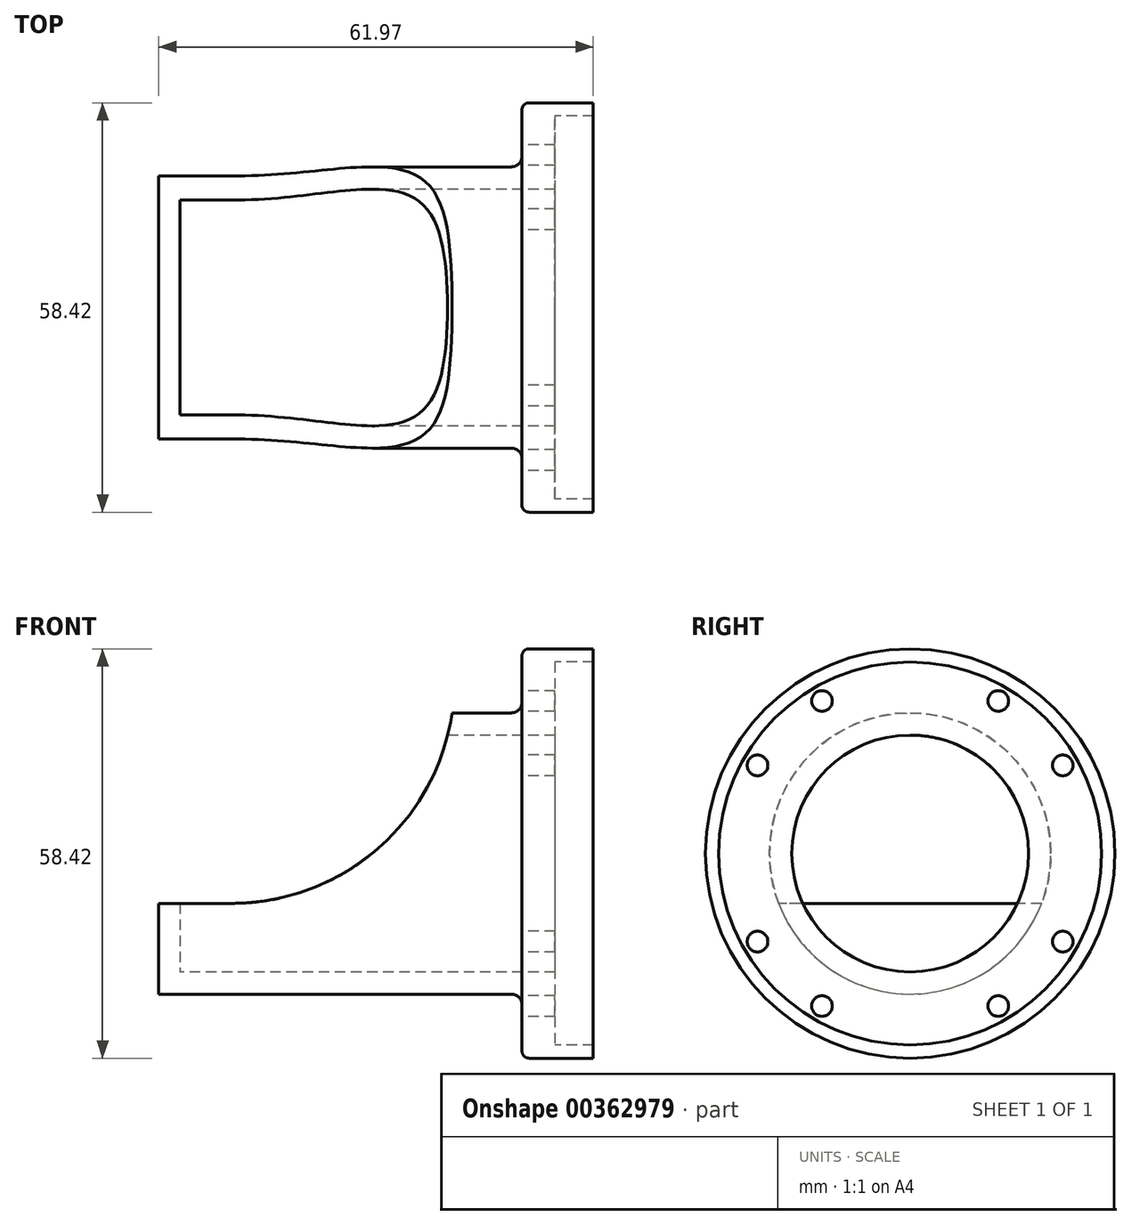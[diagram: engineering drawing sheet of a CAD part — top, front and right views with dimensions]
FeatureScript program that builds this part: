
annotation { "Feature Type Name" : "Feature", "Feature Type Description" : "" }
export const myFeature = defineFeature(function(context is Context, id is Id, definition is map)
    precondition{}
    {
        {
            var Q0;
            Q0=qCreatedBy(makeId("Front.planeOp"),FACE);
            var sketch = newSketch(context, id + "F0", { "sketchPlane" : qUnion([Q0])});
            skLineSegment(sketch, "E0", {"start": v(-33.27, -5.62) * mm, "end": v(17.02, -5.62) * mm});
            skLineSegment(sketch, "E1", {"start": v(18.54, -7.15) * mm, "end": v(18.54, -13.75) * mm});
            skLineSegment(sketch, "E2", {"start": v(19.56, -14.77) * mm, "end": v(28.7, -14.77) * mm});
            skLineSegment(sketch, "E3", {"start": v(28.7, -14.77) * mm, "end": v(28.7, -12.87) * mm});
            skLineSegment(sketch, "E4", {"start": v(28.7, -12.87) * mm, "end": v(23.24, -12.87) * mm});
            skLineSegment(sketch, "E5", {"start": v(23.24, -12.87) * mm, "end": v(23.24, -2.45) * mm});
            skLineSegment(sketch, "E6", {"start": v(23.24, -2.45) * mm, "end": v(-30.22, -2.45) * mm});
            skLineSegment(sketch, "E7", {"start": v(-30.22, -2.45) * mm, "end": v(-30.22, 12.92) * mm});
            skLineSegment(sketch, "E8", {"start": v(-30.22, 12.92) * mm, "end": v(-33.27, 12.92) * mm});
            skLineSegment(sketch, "E9", {"start": v(-33.27, 12.92) * mm, "end": v(-33.27, -5.62) * mm});
            skLineSegment(sketch, "E10", {"start": v(-34.84, 14.44) * mm, "end": v(22.49, 14.44) * mm, "construction": true});
            skPoint(sketch, "E11.visualSharp", {"position": v(18.54, -5.62) * mm});
            skArc(sketch, "E11.filletArc", {"start": v(18.54, -7.15) * mm, "mid": v(18.1, -6.07) * mm, "end": v(17.02, -5.62) * mm});
            skPoint(sketch, "E12.visualSharp", {"position": v(18.54, -14.77) * mm});
            skArc(sketch, "E12.filletArc", {"start": v(18.54, -13.75) * mm, "mid": v(18.84, -14.47) * mm, "end": v(19.56, -14.77) * mm});
            skSolve(sketch);
        }
        {
            var Q0;
            Q0=makeQuery(id+"F0.imprint","IMPRINT",FACE,{"disambiguationData":[TD([[makeQuery(id+"F0.imprint","IMPRINT",EDGE,{"derivedFrom":sQuery(id+"F0.wireOp",EDGE,"E0")}),1.0]])]});
            var Q1;
            Q1=sQuery(id+"F0.wireOp",EDGE,"E10");
            revolve(context, id + "F1", {"entities" : qUnion([Q0]), "axis" : qUnion([Q1]), "revolveType" : RevolveType.FULL});
        }
        {
            var Q0;
            Q0=qCreatedBy(makeId("Front.planeOp"),FACE);
            var sketch = newSketch(context, id + "F2", { "sketchPlane" : qUnion([Q0])});
            skLineSegment(sketch, "E13", {"start": v(8.9, 42.08) * mm, "end": v(8.9, 39.08) * mm});
            skLineSegment(sketch, "E14.0", {"start": v(-33.27, -5.62) * mm, "end": v(-33.27, 34.51) * mm});
            skLineSegment(sketch, "E15.0", {"start": v(-33.27, 7.33) * mm, "end": v(-22.86, 7.33) * mm});
            skLineSegment(sketch, "E16.0", {"start": v(18.54, -13.75) * mm, "end": v(18.54, 42.64) * mm});
            skPoint(sketch, "E17.visualSharp", {"position": v(8.9, 7.33) * mm});
            skArc(sketch, "E17.filletArc", {"start": v(-22.86, 7.33) * mm, "mid": v(-0.4, 16.63) * mm, "end": v(8.9, 39.08) * mm});
            skLineSegment(sketch, "E18", {"start": v(8.9, 42.08) * mm, "end": v(-33.27, 42.08) * mm});
            skLineSegment(sketch, "E19", {"start": v(-33.27, 42.08) * mm, "end": v(-33.27, 34.51) * mm});
            skSolve(sketch);
        }
        {
            var Q0;
            Q0=makeQuery(id+"F2.imprint","IMPRINT",FACE,{"disambiguationData":[TD([[makeQuery(id+"F2.imprint","IMPRINT",EDGE,{"derivedFrom":sQuery(id+"F2.wireOp",EDGE,"E13")}),-1.0]])]});
            extrude(context, id + "F3", {"entities" : qUnion([Q0]), "operationType" : NewBodyOperationType.REMOVE, "endBound" : BoundingType.SYMMETRIC, "oppositeDirection" : true, "depth" : 58.06 * mm});
        }
        {
            var Q0;
            Q0=makeQuery(id+"F1.opRevolve","SWEPT_FACE",FACE,{"disambiguationData":[OSD([sQuery(id+"F0.wireOp",EDGE,"E1")])]});
            var sketch = newSketch(context, id + "F4", { "sketchPlane" : qUnion([Q0])});
            skPoint(sketch, "E20", {"position": v(12.57, 36.21) * mm});
            skPoint(sketch, "E21", {"position": v(21.77, 27.02) * mm});
            skCircle(sketch, "E22.0", {"center": v(0, 14.44) * mm, "radius": 21.6 * mm});
            skPoint(sketch, "E23.1.0", {"position": v(-12.57, 36.21) * mm});
            skPoint(sketch, "E23.1.1", {"position": v(-21.77, 27.02) * mm});
            skPoint(sketch, "E23.2.0", {"position": v(-21.77, 1.87) * mm});
            skPoint(sketch, "E23.2.1", {"position": v(-12.57, -7.32) * mm});
            skPoint(sketch, "E23.3.0", {"position": v(12.57, -7.32) * mm});
            skPoint(sketch, "E23.3.1", {"position": v(21.77, 1.87) * mm});
            skSolve(sketch);
        }
        {
            var Q0;
            Q0=sQuery(id+"F4.wireOp",VERTEX,"E20");
            var Q1;
            Q1=sQuery(id+"F4.wireOp",VERTEX,"E21");
            var Q2;
            Q2=sQuery(id+"F4.wireOp",VERTEX,"E23.1.0");
            var Q3;
            Q3=sQuery(id+"F4.wireOp",VERTEX,"E23.1.1");
            var Q4;
            Q4=sQuery(id+"F4.wireOp",VERTEX,"E23.3.1");
            var Q5;
            Q5=sQuery(id+"F4.wireOp",VERTEX,"E23.3.0");
            var Q6;
            Q6=sQuery(id+"F4.wireOp",VERTEX,"E23.2.1");
            var Q7;
            Q7=sQuery(id+"F4.wireOp",VERTEX,"E23.2.0");
            var Q8;
            Q8=makeQuery(id+"F1.opRevolve","SWEPT_BODY",BODY,{"disambiguationData":[OSD([sQuery(id+"F0.wireOp",EDGE,"E0"),sQuery(id+"F0.wireOp",EDGE,"E1"),sQuery(id+"F0.wireOp",EDGE,"E2"),sQuery(id+"F0.wireOp",EDGE,"E3"),sQuery(id+"F0.wireOp",EDGE,"E4"),sQuery(id+"F0.wireOp",EDGE,"E5"),sQuery(id+"F0.wireOp",EDGE,"E6"),sQuery(id+"F0.wireOp",EDGE,"E7"),sQuery(id+"F0.wireOp",EDGE,"E8"),sQuery(id+"F0.wireOp",EDGE,"E9"),sQuery(id+"F0.wireOp",EDGE,"E11.filletArc"),sQuery(id+"F0.wireOp",EDGE,"E12.filletArc")])]});
            hole(context, id + "F5", {"style" : HoleStyle.SIMPLE, "endStyle" : HoleEndStyle.THROUGH, "standardTappedOrClearance" : lookupTablePath({ "standard" : "ANSI", "size" : "#32 (0.12)", "type" : "Drilled" }), "standardBlindInLast" : lookupTablePath({ "standard" : "ANSI", "size" : "#32", "type" : "Drilled" }), "holeDiameter" : 2.95 * mm, "tappedDepth" : 5.4 * mm, "tapClearance" : 3, "locations" : qUnion([Q0, Q1, Q2, Q3, Q4, Q5, Q6, Q7]), "scope" : qUnion([Q8])});
        }
    });
